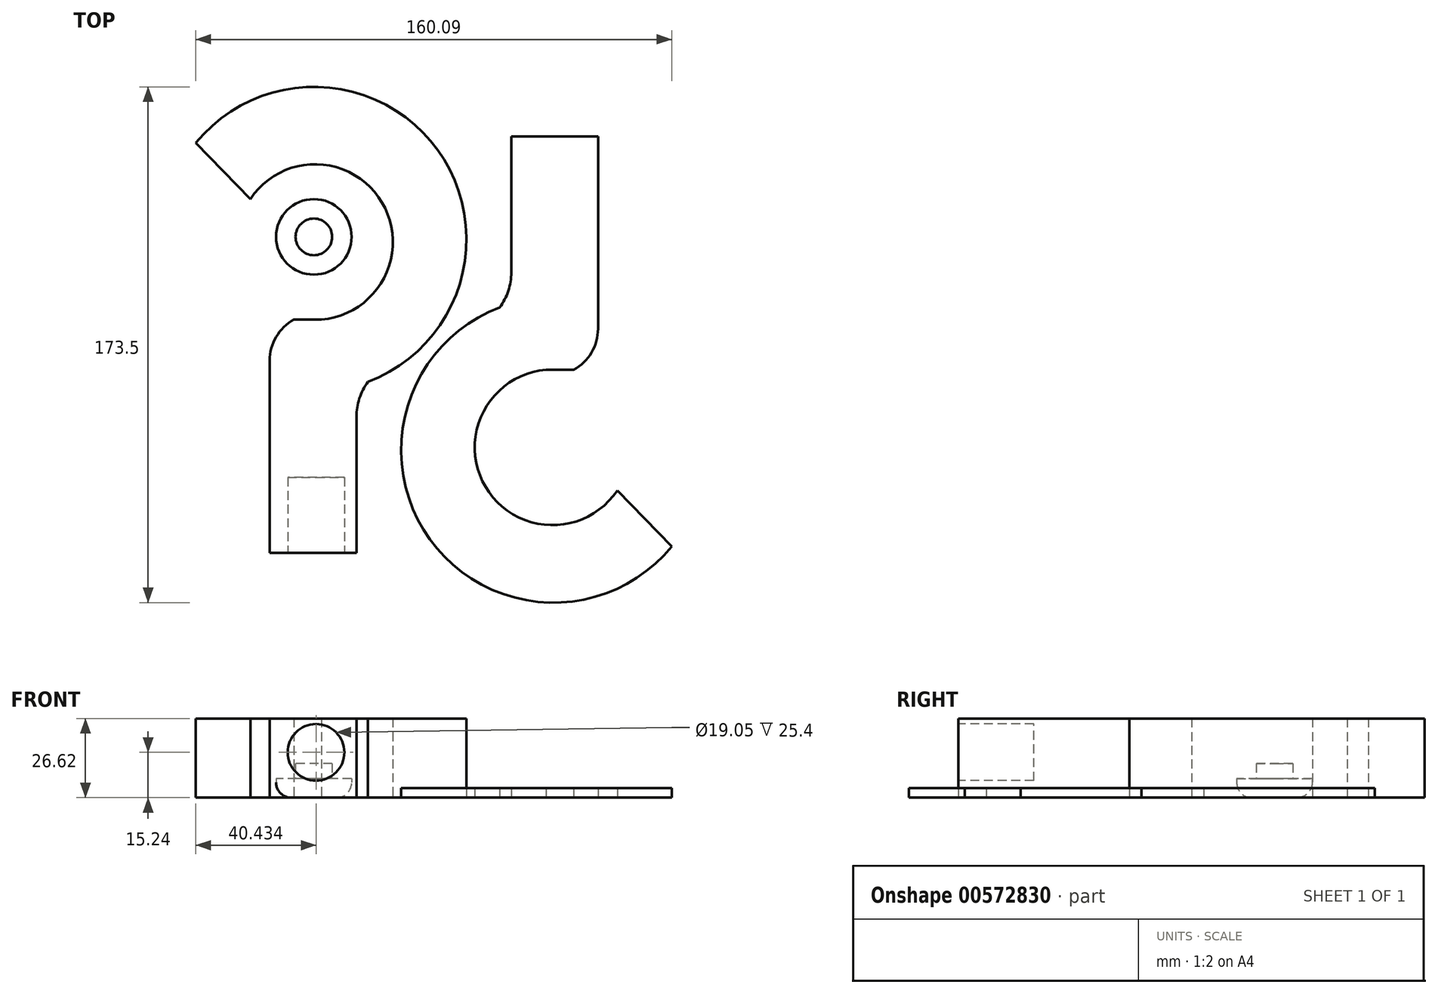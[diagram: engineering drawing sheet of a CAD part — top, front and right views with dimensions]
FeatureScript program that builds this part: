
annotation { "Feature Type Name" : "Feature", "Feature Type Description" : "" }
export const myFeature = defineFeature(function(context is Context, id is Id, definition is map)
    precondition{}
    {
        {
            var Q0;
            Q0=qCreatedBy(makeId("Top.planeOp"),FACE);
            var sketch = newSketch(context, id + "F0", { "sketchPlane" : qUnion([Q0])});
            skArc(sketch, "E0", {"start": v(-11.76, 4.51) * mm, "mid": v(8.62, 43.88) * mm, "end": v(-35.7, 45.06) * mm});
            skLineSegment(sketch, "E1", {"start": v(-35.7, 45.06) * mm, "end": v(-54.03, 63.89) * mm});
            skArc(sketch, "E2", {"start": v(3.89, -16.45) * mm, "mid": v(27.34, 61.5) * mm, "end": v(-54.03, 63.89) * mm});
            skLineSegment(sketch, "E3", {"start": v(0, -28.26) * mm, "end": v(0, -73.99) * mm});
            skLineSegment(sketch, "E4", {"start": v(-11.76, 4.51) * mm, "end": v(-21, 4.51) * mm});
            skLineSegment(sketch, "E5", {"start": v(0, -73.99) * mm, "end": v(-29.2, -73.99) * mm});
            skLineSegment(sketch, "E6", {"start": v(-29.2, -73.99) * mm, "end": v(-29.2, -9.34) * mm});
            skArc(sketch, "E7", {"start": v(-21, 4.51) * mm, "mid": v(-26.99, -1.3) * mm, "end": v(-29.2, -9.34) * mm});
            skArc(sketch, "E8", {"start": v(3.89, -16.45) * mm, "mid": v(1, -22.05) * mm, "end": v(0, -28.26) * mm});
            skSolve(sketch);
        }
        {
            var Q0;
            Q0=makeQuery(id+"F0.imprint","IMPRINT",FACE,{"disambiguationData":[TD([[makeQuery(id+"F0.imprint","IMPRINT",EDGE,{"derivedFrom":sQuery(id+"F0.wireOp",EDGE,"E0")}),-1.0]])]});
            extrude(context, id + "F1", {"entities" : qUnion([Q0]), "depth" : 30.48 * mm, "offsetDistance" : 25.4 * mm});
        }
        {
            var Q0;
            Q0=makeQuery(id+"F1.opExtrude","SWEPT_FACE",FACE,{"disambiguationData":[OSD([sQuery(id+"F0.wireOp",EDGE,"E5")])]});
            var sketch = newSketch(context, id + "F2", { "sketchPlane" : qUnion([Q0])});
            skCircle(sketch, "E9", {"center": v(-13.6, 15.24) * mm, "radius": 9.53 * mm});
            skPoint(sketch, "E9.centerSnap0", {"position": v(0, 15.24) * mm});
            skSolve(sketch);
        }
        {
            var Q0;
            Q0=makeQuery(id+"F2.imprint","IMPRINT",FACE,{"disambiguationData":[TD([[makeQuery(id+"F2.imprint","IMPRINT",EDGE,{"derivedFrom":sQuery(id+"F2.wireOp",EDGE,"E9")}),1.0]])]});
            extrude(context, id + "F3", {"entities" : qUnion([Q0]), "operationType" : NewBodyOperationType.REMOVE, "oppositeDirection" : true, "depth" : 25.4 * mm, "offsetDistance" : 25.4 * mm});
        }
        {
            var Q0;
            Q0=qCreatedBy(makeId("Top.planeOp"),FACE);
            cPlane(context, id + "F4", {"entities" : qUnion([Q0]), "cplaneType" : CPlaneType.OFFSET, "offset" : 34.54 * mm, "width" : 152.4 * mm, "height" : 152.4 * mm});
        }
        {
            var Q0;
            Q0=qCreatedBy(id+"F4.planeOp",FACE);
            var sketch = newSketch(context, id + "F5", { "sketchPlane" : qUnion([Q0])});
            skLineSegment(sketch, "E10.bottom", {"start": v(-68.13, 86.44) * mm, "end": v(40.44, 86.44) * mm});
            skLineSegment(sketch, "E10.top", {"start": v(-68.13, -103.55) * mm, "end": v(40.44, -103.55) * mm});
            skLineSegment(sketch, "E10.left", {"start": v(-68.13, 86.44) * mm, "end": v(-68.13, -103.55) * mm});
            skLineSegment(sketch, "E10.right", {"start": v(40.44, 86.44) * mm, "end": v(40.44, -103.55) * mm});
            skSolve(sketch);
        }
        {
            var Q0;
            Q0=makeQuery(id+"F5.imprint","IMPRINT",FACE,{"disambiguationData":[TD([[makeQuery(id+"F5.imprint","IMPRINT",EDGE,{"derivedFrom":sQuery(id+"F5.wireOp",EDGE,"E10.bottom")}),-1.0]])]});
            extrude(context, id + "F6", {"entities" : qUnion([Q0]), "operationType" : NewBodyOperationType.REMOVE, "oppositeDirection" : true, "depth" : 7.92 * mm, "offsetDistance" : 25.4 * mm});
        }
        {
            var Q0;
            Q0=qCreatedBy(makeId("Top.planeOp"),FACE);
            var sketch = newSketch(context, id + "F7", { "sketchPlane" : qUnion([Q0])});
            skCircle(sketch, "E11", {"center": v(-14.31, 32.31) * mm, "radius": 12.7 * mm});
            skSolve(sketch);
        }
        {
            var Q0;
            Q0=makeQuery(id+"F7.imprint","IMPRINT",FACE,{"disambiguationData":[TD([[makeQuery(id+"F7.imprint","IMPRINT",EDGE,{"derivedFrom":sQuery(id+"F7.wireOp",EDGE,"E11")}),1.0]])]});
            extrude(context, id + "F8", {"entities" : qUnion([Q0]), "depth" : 6.35 * mm, "offsetDistance" : 25.4 * mm});
        }
        {
            var Q0;
            Q0=makeQuery(id+"F8.opExtrude","CAP_FACE",FACE,{"disambiguationData":[OSD([sQuery(id+"F7.wireOp",EDGE,"E11")])],"isStart":false});
            var sketch = newSketch(context, id + "F9", { "sketchPlane" : qUnion([Q0])});
            skCircle(sketch, "E12", {"center": v(-14.31, 32.31) * mm, "radius": 6.16 * mm});
            skSolve(sketch);
        }
        {
            var Q0;
            Q0=makeQuery(id+"F9.imprint","IMPRINT",FACE,{"disambiguationData":[TD([[makeQuery(id+"F9.imprint","IMPRINT",EDGE,{"derivedFrom":sQuery(id+"F9.wireOp",EDGE,"E12")}),1.0]])]});
            extrude(context, id + "F10", {"entities" : qUnion([Q0]), "operationType" : NewBodyOperationType.ADD, "depth" : 5.08 * mm, "offsetDistance" : 25.4 * mm});
        }
        {
            var Q0;
            Q0=makeQuery(id+"F8.opExtrude","CAP_EDGE",EDGE,{"disambiguationData":[OSD([sQuery(id+"F7.wireOp",EDGE,"E11")])],"isStart":true});
            fillet(context, id + "F11", {"entities" : qUnion([Q0]), "radius" : 5.08 * mm, "tangentPropagation" : true, "allowEdgeOverflow" : false});
        }
        {
            var Q0;
            Q0=qCreatedBy(makeId("Top.planeOp"),FACE);
            var sketch = newSketch(context, id + "F12", { "sketchPlane" : qUnion([Q0])});
            skArc(sketch, "E13", {"start": v(63.83, -12.42) * mm, "mid": v(43.43, -51.78) * mm, "end": v(87.74, -52.99) * mm});
            skLineSegment(sketch, "E14", {"start": v(87.74, -52.99) * mm, "end": v(106.06, -71.83) * mm});
            skArc(sketch, "E15", {"start": v(48.2, 8.55) * mm, "mid": v(24.7, -69.38) * mm, "end": v(106.06, -71.83) * mm});
            skLineSegment(sketch, "E16", {"start": v(52.1, 20.36) * mm, "end": v(52.13, 66.08) * mm});
            skLineSegment(sketch, "E17", {"start": v(63.83, -12.42) * mm, "end": v(73.06, -12.43) * mm});
            skLineSegment(sketch, "E18", {"start": v(52.13, 66.08) * mm, "end": v(81.32, 66.06) * mm});
            skLineSegment(sketch, "E19", {"start": v(81.32, 66.06) * mm, "end": v(81.27, 1.42) * mm});
            skArc(sketch, "E20", {"start": v(73.06, -12.43) * mm, "mid": v(79.06, -6.63) * mm, "end": v(81.27, 1.42) * mm});
            skArc(sketch, "E21", {"start": v(48.2, 8.55) * mm, "mid": v(51.1, 14.15) * mm, "end": v(52.1, 20.36) * mm});
            skSolve(sketch);
        }
        {
            var Q0;
            Q0=makeQuery(id+"F12.imprint","IMPRINT",FACE,{"disambiguationData":[TD([[makeQuery(id+"F12.imprint","IMPRINT",EDGE,{"derivedFrom":sQuery(id+"F12.wireOp",EDGE,"E13")}),-1.0]])]});
            extrude(context, id + "F13", {"entities" : qUnion([Q0]), "depth" : 3.17 * mm, "offsetDistance" : 25.4 * mm});
        }
    });
